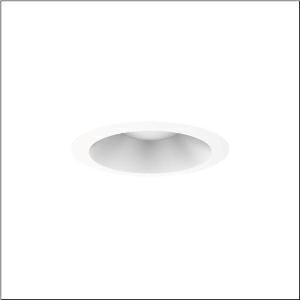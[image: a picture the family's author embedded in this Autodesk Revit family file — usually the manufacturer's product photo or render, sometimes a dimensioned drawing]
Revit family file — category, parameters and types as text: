
# Revit family: lunis_31_midi_51dn157g32
name_source: partatom
category: Lighting Fixtures
units: mm (PartAtom-declared; Revit-internal decimal feet)

## family parameters
Cut with Voids When Loaded = No
Host = Face
Light Source = No
Part Type = Normal
Room Calculation Point = No
Round Connector Dimension = Use Diameter
Shared = No

## types (1)
- Lunis 31 midi (1 x LED, 2000 lm, 17 W, 3000K)
    Apparent Load = 17 VA
    CIE Flux Codes = 89 99 100 100 100
    Color Rendering = 80
    Color Temperature = 3000K
    Default Elevation = 1800 mm
    Description = Lunis 31,  midi, downlight, light control with lens, light emission: direct distribution, LED rated luminous flux: 2.000lm, light colour: 830, mains connection: 220..240V, AC, 50/60Hz, housing, white, protection rating (complete): IP20, protection rating (on room side): IP54, insulation class (complete): insulation class II (safety insulation), certification: CE, packaging unit: 1 piece
    Height = 0 mm  [stored 0 ft]
    Lamp = 1 x LED
    Lamp Light Flux = 2000 lm
    Lamp Power = 17 W
    Lamp count = 1
    Length = 259 mm
    Luminous efficacy = 118 lm/W
    Manufacturer = Siteco
    ModVariant = No
    Model = 51DN157G32
    Mounting Place = Ceiling
    Mounting Type = Recessed
    Number of Poles = 1
    OnlyDefault = Yes
    Power Factor = 1
    Product Name = Lunis 31 midi
    Product group = downlight
    ProductGroupID = 400
    Protection Class = Protection class II
    Protection Degree = IP 20
    RLX_Detail_Level = 1
    RLX_Emergency_Light_Flux = 0 lm
    RLX_Emergency_Type = 0
    RLX_Emergency_Type_DB = No
    RlxData = <blob elided: 23741 chars, md5=970d635f>
    Socket = socket
    Standby Power = 0 W
    System Light Flux = 2000 lm
    System Power = 17 W
    Type Comments = Product without accessories
    Type Image = l_1006711.jpg
    URL = http://relux.com
    VarID = ---
    Voltage = 0 V
    Weight = 0.00 kg
    Width = 0 mm  [stored 0 ft]

note: [stored X ft] marks values corroborated as IEEE doubles in the binary element streams (Revit-internal decimal feet)

## geometry (parser evidence)
native form markers: Blend x4, Sweep x12
no freeform markers — native parametric forms only
